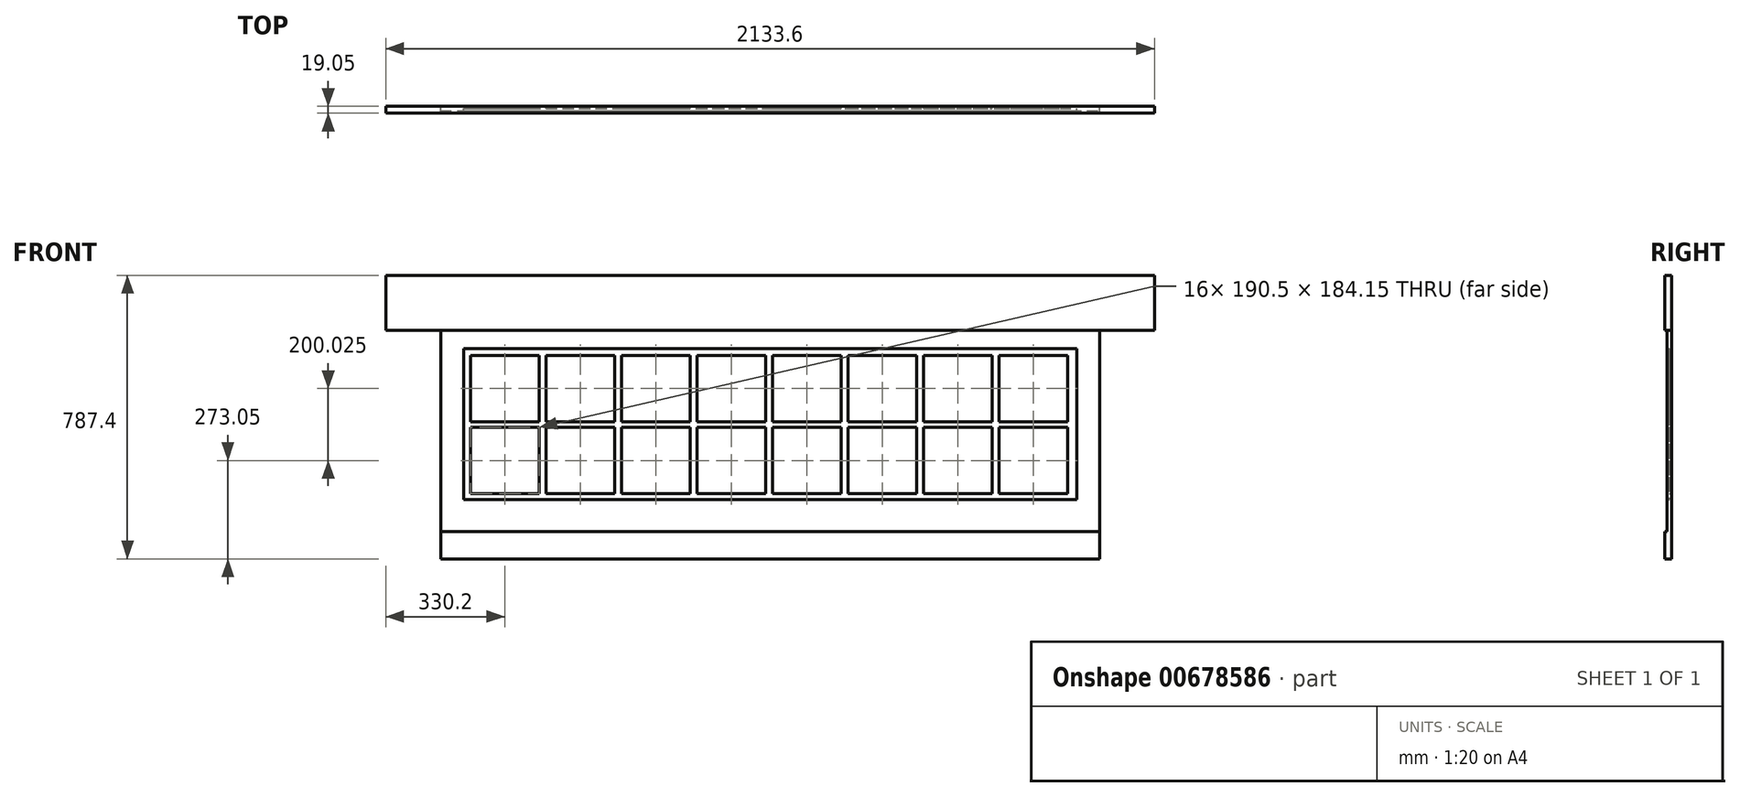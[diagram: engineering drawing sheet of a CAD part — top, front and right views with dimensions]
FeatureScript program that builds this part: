
annotation { "Feature Type Name" : "Feature", "Feature Type Description" : "" }
export const myFeature = defineFeature(function(context is Context, id is Id, definition is map)
    precondition{}
    {
        {
            var Q0;
            Q0=qCreatedBy(makeId("Front.planeOp"),FACE);
            var sketch = newSketch(context, id + "F0", { "sketchPlane" : qUnion([Q0])});
            skLineSegment(sketch, "E0.bottom", {"start": v(-1066.8, 1447.8) * mm, "end": v(1066.8, 1447.8) * mm});
            skLineSegment(sketch, "E0.top", {"start": v(-1066.8, -1447.8) * mm, "end": v(1066.8, -1447.8) * mm});
            skLineSegment(sketch, "E0.left", {"start": v(-1066.8, 1447.8) * mm, "end": v(-1066.8, -1447.8) * mm});
            skLineSegment(sketch, "E0.right", {"start": v(1066.8, 1447.8) * mm, "end": v(1066.8, -1447.8) * mm});
            skPoint(sketch, "E0.middle", {"position": v(0, 0) * mm});
            skLineSegment(sketch, "E1.bottom", {"start": v(-1066.8, -1447.8) * mm, "end": v(-914.4, -1447.8) * mm});
            skLineSegment(sketch, "E1.top", {"start": v(-1066.8, 1447.8) * mm, "end": v(-914.4, 1447.8) * mm});
            skLineSegment(sketch, "E1.left", {"start": v(-1066.8, -1447.8) * mm, "end": v(-1066.8, 1447.8) * mm});
            skLineSegment(sketch, "E1.right", {"start": v(-914.4, -1447.8) * mm, "end": v(-914.4, 1447.8) * mm});
            skLineSegment(sketch, "E2.bottom", {"start": v(1066.8, 1447.8) * mm, "end": v(914.4, 1447.8) * mm});
            skLineSegment(sketch, "E2.top", {"start": v(1066.8, -1447.8) * mm, "end": v(914.4, -1447.8) * mm});
            skLineSegment(sketch, "E2.right", {"start": v(914.4, 1447.8) * mm, "end": v(914.4, -1447.8) * mm});
            skLineSegment(sketch, "E3", {"start": v(-914.4, 660.4) * mm, "end": v(914.4, 660.4) * mm});
            skLineSegment(sketch, "E4", {"start": v(-914.4, 736.6) * mm, "end": v(914.4, 736.6) * mm});
            skLineSegment(sketch, "E5", {"start": v(-1066.8, 1295.4) * mm, "end": v(1066.8, 1295.4) * mm});
            skLineSegment(sketch, "E6.bottom", {"start": v(-850.9, 1244.6) * mm, "end": v(850.9, 1244.6) * mm});
            skLineSegment(sketch, "E6.top", {"start": v(-850.9, 825.5) * mm, "end": v(850.9, 825.5) * mm});
            skLineSegment(sketch, "E6.left", {"start": v(-850.9, 1244.6) * mm, "end": v(-850.9, 825.5) * mm});
            skLineSegment(sketch, "E6.right", {"start": v(850.9, 1244.6) * mm, "end": v(850.9, 825.5) * mm});
            skPoint(sketch, "E7.orphan", {"position": v(1066.8, 736.6) * mm});
            skPoint(sketch, "E8.orphan", {"position": v(1066.8, 660.4) * mm});
            skLineSegment(sketch, "E9.bottom", {"start": v(-831.85, 1041.4) * mm, "end": v(-641.35, 1041.4) * mm});
            skLineSegment(sketch, "E9.top", {"start": v(-831.85, 1025.53) * mm, "end": v(-641.35, 1025.53) * mm});
            skLineSegment(sketch, "E9.left", {"start": v(-850.9, 1041.4) * mm, "end": v(-850.9, 1025.53) * mm});
            skLineSegment(sketch, "E9.right", {"start": v(850.9, 1041.4) * mm, "end": v(850.9, 1025.53) * mm});
            skLineSegment(sketch, "E10.bottom", {"start": v(-641.35, 1244.6) * mm, "end": v(-622.3, 1244.6) * mm});
            skLineSegment(sketch, "E10.top", {"start": v(-641.35, 825.5) * mm, "end": v(-622.3, 825.5) * mm});
            skLineSegment(sketch, "E10.left", {"start": v(-641.35, 1225.55) * mm, "end": v(-641.35, 1041.4) * mm});
            skLineSegment(sketch, "E10.right", {"start": v(-622.3, 1225.55) * mm, "end": v(-622.3, 841.38) * mm});
            skLineSegment(sketch, "E11.top", {"start": v(-831.85, 1225.55) * mm, "end": v(-641.35, 1225.55) * mm});
            skLineSegment(sketch, "E11.left", {"start": v(-850.9, 1244.6) * mm, "end": v(-850.9, 1225.55) * mm});
            skLineSegment(sketch, "E11.right", {"start": v(850.9, 1244.6) * mm, "end": v(850.9, 1225.55) * mm});
            skLineSegment(sketch, "E12.bottom", {"start": v(850.9, 825.5) * mm, "end": v(-850.9, 825.5) * mm});
            skLineSegment(sketch, "E12.top", {"start": v(850.9, 841.38) * mm, "end": v(-831.85, 841.38) * mm});
            skLineSegment(sketch, "E12.left", {"start": v(850.9, 825.5) * mm, "end": v(850.9, 841.38) * mm});
            skLineSegment(sketch, "E12.right", {"start": v(-850.9, 825.5) * mm, "end": v(-850.9, 841.38) * mm});
            skLineSegment(sketch, "E13.bottom", {"start": v(-850.9, 1244.6) * mm, "end": v(-831.85, 1244.6) * mm});
            skLineSegment(sketch, "E13.top", {"start": v(-850.9, 825.5) * mm, "end": v(-831.85, 825.5) * mm});
            skLineSegment(sketch, "E13.right", {"start": v(-831.85, 1225.55) * mm, "end": v(-831.85, 841.38) * mm});
            skLineSegment(sketch, "E14.bottom", {"start": v(-622.3, 1225.55) * mm, "end": v(-431.8, 1225.55) * mm});
            skLineSegment(sketch, "E14.top", {"start": v(-622.3, 1041.4) * mm, "end": v(-431.8, 1041.4) * mm});
            skLineSegment(sketch, "E14.left", {"start": v(-622.3, 1225.55) * mm, "end": v(-622.3, 1041.4) * mm});
            skLineSegment(sketch, "E14.right", {"start": v(-431.8, 1225.55) * mm, "end": v(-431.8, 1041.4) * mm});
            skLineSegment(sketch, "E15.bottom", {"start": v(-412.75, 1225.55) * mm, "end": v(-222.25, 1225.55) * mm});
            skLineSegment(sketch, "E15.top", {"start": v(-412.75, 1041.4) * mm, "end": v(-222.25, 1041.4) * mm});
            skLineSegment(sketch, "E15.left", {"start": v(-412.75, 1225.55) * mm, "end": v(-412.75, 1041.4) * mm});
            skLineSegment(sketch, "E15.right", {"start": v(-222.25, 1225.55) * mm, "end": v(-222.25, 1041.4) * mm});
            skLineSegment(sketch, "E16.bottom", {"start": v(-203.2, 1225.55) * mm, "end": v(-12.7, 1225.55) * mm});
            skLineSegment(sketch, "E16.top", {"start": v(-203.2, 1041.4) * mm, "end": v(-12.7, 1041.4) * mm});
            skLineSegment(sketch, "E16.left", {"start": v(-203.2, 1225.55) * mm, "end": v(-203.2, 1041.4) * mm});
            skLineSegment(sketch, "E16.right", {"start": v(-12.7, 1225.55) * mm, "end": v(-12.7, 1041.4) * mm});
            skLineSegment(sketch, "E17.bottom", {"start": v(6.35, 1225.55) * mm, "end": v(196.85, 1225.55) * mm});
            skLineSegment(sketch, "E17.top", {"start": v(6.35, 1041.4) * mm, "end": v(196.85, 1041.4) * mm});
            skLineSegment(sketch, "E17.left", {"start": v(6.35, 1225.55) * mm, "end": v(6.35, 1041.4) * mm});
            skLineSegment(sketch, "E17.right", {"start": v(196.85, 1225.55) * mm, "end": v(196.85, 1041.4) * mm});
            skLineSegment(sketch, "E18.bottom", {"start": v(215.9, 1225.55) * mm, "end": v(406.4, 1225.55) * mm});
            skLineSegment(sketch, "E18.top", {"start": v(215.9, 1041.4) * mm, "end": v(406.4, 1041.4) * mm});
            skLineSegment(sketch, "E18.left", {"start": v(215.9, 1225.55) * mm, "end": v(215.9, 1041.4) * mm});
            skLineSegment(sketch, "E18.right", {"start": v(406.4, 1225.55) * mm, "end": v(406.4, 1041.4) * mm});
            skLineSegment(sketch, "E19.bottom", {"start": v(-622.3, 1025.53) * mm, "end": v(-431.8, 1025.53) * mm});
            skLineSegment(sketch, "E19.top", {"start": v(-622.3, 841.38) * mm, "end": v(-431.8, 841.38) * mm});
            skLineSegment(sketch, "E19.left", {"start": v(-622.3, 1025.53) * mm, "end": v(-622.3, 841.38) * mm});
            skLineSegment(sketch, "E19.right", {"start": v(-431.8, 1025.53) * mm, "end": v(-431.8, 841.38) * mm});
            skLineSegment(sketch, "E20.bottom", {"start": v(-412.75, 1025.53) * mm, "end": v(-222.25, 1025.53) * mm});
            skLineSegment(sketch, "E20.top", {"start": v(-412.75, 841.38) * mm, "end": v(-222.25, 841.38) * mm});
            skLineSegment(sketch, "E20.left", {"start": v(-412.75, 1025.53) * mm, "end": v(-412.75, 841.38) * mm});
            skLineSegment(sketch, "E20.right", {"start": v(-222.25, 1025.53) * mm, "end": v(-222.25, 841.38) * mm});
            skLineSegment(sketch, "E21.bottom", {"start": v(-203.2, 1025.53) * mm, "end": v(-12.7, 1025.53) * mm});
            skLineSegment(sketch, "E21.top", {"start": v(-203.2, 841.38) * mm, "end": v(-12.7, 841.38) * mm});
            skLineSegment(sketch, "E21.left", {"start": v(-203.2, 1025.53) * mm, "end": v(-203.2, 841.38) * mm});
            skLineSegment(sketch, "E21.right", {"start": v(-12.7, 1025.53) * mm, "end": v(-12.7, 841.38) * mm});
            skLineSegment(sketch, "E22.bottom", {"start": v(6.35, 1025.53) * mm, "end": v(196.85, 1025.53) * mm});
            skLineSegment(sketch, "E22.top", {"start": v(6.35, 841.38) * mm, "end": v(196.85, 841.38) * mm});
            skLineSegment(sketch, "E22.left", {"start": v(6.35, 1025.53) * mm, "end": v(6.35, 841.38) * mm});
            skLineSegment(sketch, "E22.right", {"start": v(196.85, 1025.53) * mm, "end": v(196.85, 841.38) * mm});
            skLineSegment(sketch, "E23.bottom", {"start": v(215.9, 1025.53) * mm, "end": v(406.4, 1025.53) * mm});
            skLineSegment(sketch, "E23.top", {"start": v(215.9, 841.38) * mm, "end": v(406.4, 841.38) * mm});
            skLineSegment(sketch, "E23.left", {"start": v(215.9, 1025.53) * mm, "end": v(215.9, 841.38) * mm});
            skLineSegment(sketch, "E23.right", {"start": v(406.4, 1025.53) * mm, "end": v(406.4, 841.38) * mm});
            skLineSegment(sketch, "E24.bottom", {"start": v(425.45, 1225.55) * mm, "end": v(615.95, 1225.55) * mm});
            skLineSegment(sketch, "E24.top", {"start": v(425.45, 1041.4) * mm, "end": v(615.95, 1041.4) * mm});
            skLineSegment(sketch, "E24.left", {"start": v(425.45, 1225.55) * mm, "end": v(425.45, 1041.4) * mm});
            skLineSegment(sketch, "E24.right", {"start": v(615.95, 1225.55) * mm, "end": v(615.95, 1041.4) * mm});
            skLineSegment(sketch, "E25.bottom", {"start": v(635, 1225.55) * mm, "end": v(825.5, 1225.55) * mm});
            skLineSegment(sketch, "E25.top", {"start": v(635, 1041.4) * mm, "end": v(825.5, 1041.4) * mm});
            skLineSegment(sketch, "E25.left", {"start": v(635, 1225.55) * mm, "end": v(635, 1041.4) * mm});
            skLineSegment(sketch, "E25.right", {"start": v(825.5, 1225.55) * mm, "end": v(825.5, 1041.4) * mm});
            skLineSegment(sketch, "E26.bottom", {"start": v(425.45, 1025.53) * mm, "end": v(615.95, 1025.53) * mm});
            skLineSegment(sketch, "E26.top", {"start": v(425.45, 841.38) * mm, "end": v(615.95, 841.38) * mm});
            skLineSegment(sketch, "E26.left", {"start": v(425.45, 1025.53) * mm, "end": v(425.45, 841.38) * mm});
            skLineSegment(sketch, "E26.right", {"start": v(615.95, 1025.53) * mm, "end": v(615.95, 841.38) * mm});
            skLineSegment(sketch, "E27.bottom", {"start": v(635, 1025.53) * mm, "end": v(825.5, 1025.53) * mm});
            skLineSegment(sketch, "E27.top", {"start": v(635, 841.38) * mm, "end": v(825.5, 841.38) * mm});
            skLineSegment(sketch, "E27.left", {"start": v(635, 1025.53) * mm, "end": v(635, 841.38) * mm});
            skLineSegment(sketch, "E27.right", {"start": v(825.5, 1025.53) * mm, "end": v(825.5, 841.38) * mm});
            skLineSegment(sketch, "E28.trimOffspring", {"start": v(-641.35, 1025.53) * mm, "end": v(-641.35, 841.38) * mm});
            skSolve(sketch);
        }
        {
            var Q0;
            {var subQ1=sQuery(id+"F0.wireOp",EDGE,"E1.bottom");Q0=makeQuery(id+"F0.imprint","IMPRINT",FACE,{"disambiguationData":[TD([[makeQuery(id+"F0.imprint","IMPRINT",EDGE,{"derivedFrom":subQ1}),1.0]])]});}
            var Q1;
            {var subQ0=sQuery(id+"F0.wireOp",EDGE,"E1.top");Q1=makeQuery(id+"F0.imprint","IMPRINT",FACE,{"disambiguationData":[TD([[makeQuery(id+"F0.imprint","IMPRINT",EDGE,{"derivedFrom":subQ0}),-1.0]])]});}
            var Q2;
            {var subQ0=sQuery(id+"F0.wireOp",EDGE,"E0.bottom");Q2=makeQuery(id+"F0.imprint","IMPRINT",FACE,{"disambiguationData":[TD([[makeQuery(id+"F0.imprint","IMPRINT",EDGE,{"derivedFrom":subQ0}),-1.0]])]});}
            var Q3;
            {var subQ0=sQuery(id+"F0.wireOp",EDGE,"E2.bottom");Q3=makeQuery(id+"F0.imprint","IMPRINT",FACE,{"disambiguationData":[TD([[makeQuery(id+"F0.imprint","IMPRINT",EDGE,{"derivedFrom":subQ0}),1.0]])]});}
            var Q4;
            {var subQ5=sQuery(id+"F0.wireOp",EDGE,"E2.top");Q4=makeQuery(id+"F0.imprint","IMPRINT",FACE,{"disambiguationData":[TD([[makeQuery(id+"F0.imprint","IMPRINT",EDGE,{"derivedFrom":subQ5}),-1.0]])]});}
            var Q5;
            {var subQ0=sQuery(id+"F0.wireOp",EDGE,"E3");Q5=makeQuery(id+"F0.imprint","IMPRINT",FACE,{"disambiguationData":[TD([[makeQuery(id+"F0.imprint","IMPRINT",EDGE,{"derivedFrom":subQ0}),1.0]])]});}
            extrude(context, id + "F1", {"entities" : qUnion([Q0, Q1, Q2, Q3, Q4, Q5]), "depth" : 19.05 * mm, "offsetDistance" : 25.4 * mm});
        }
        {
            var Q0;
            {var subQ5=sQuery(id+"F0.wireOp",EDGE,"E4");Q0=makeQuery(id+"F0.imprint","IMPRINT",FACE,{"disambiguationData":[TD([[makeQuery(id+"F0.imprint","IMPRINT",EDGE,{"derivedFrom":subQ5}),1.0]])]});}
            extrude(context, id + "F2", {"entities" : qUnion([Q0]), "operationType" : NewBodyOperationType.ADD, "depth" : 12.7 * mm, "offsetDistance" : 25.4 * mm});
        }
        {
            var Q0;
            {var subQ4=sQuery(id+"F0.wireOp",EDGE,"E9.bottom");Q0=makeQuery(id+"F0.imprint","IMPRINT",FACE,{"disambiguationData":[TD([[makeQuery(id+"F0.imprint","IMPRINT",EDGE,{"derivedFrom":subQ4}),-1.0]])]});}
            extrude(context, id + "F3", {"entities" : qUnion([Q0]), "operationType" : NewBodyOperationType.ADD, "depth" : 6.35 * mm, "offsetDistance" : 25.4 * mm});
        }
    });
